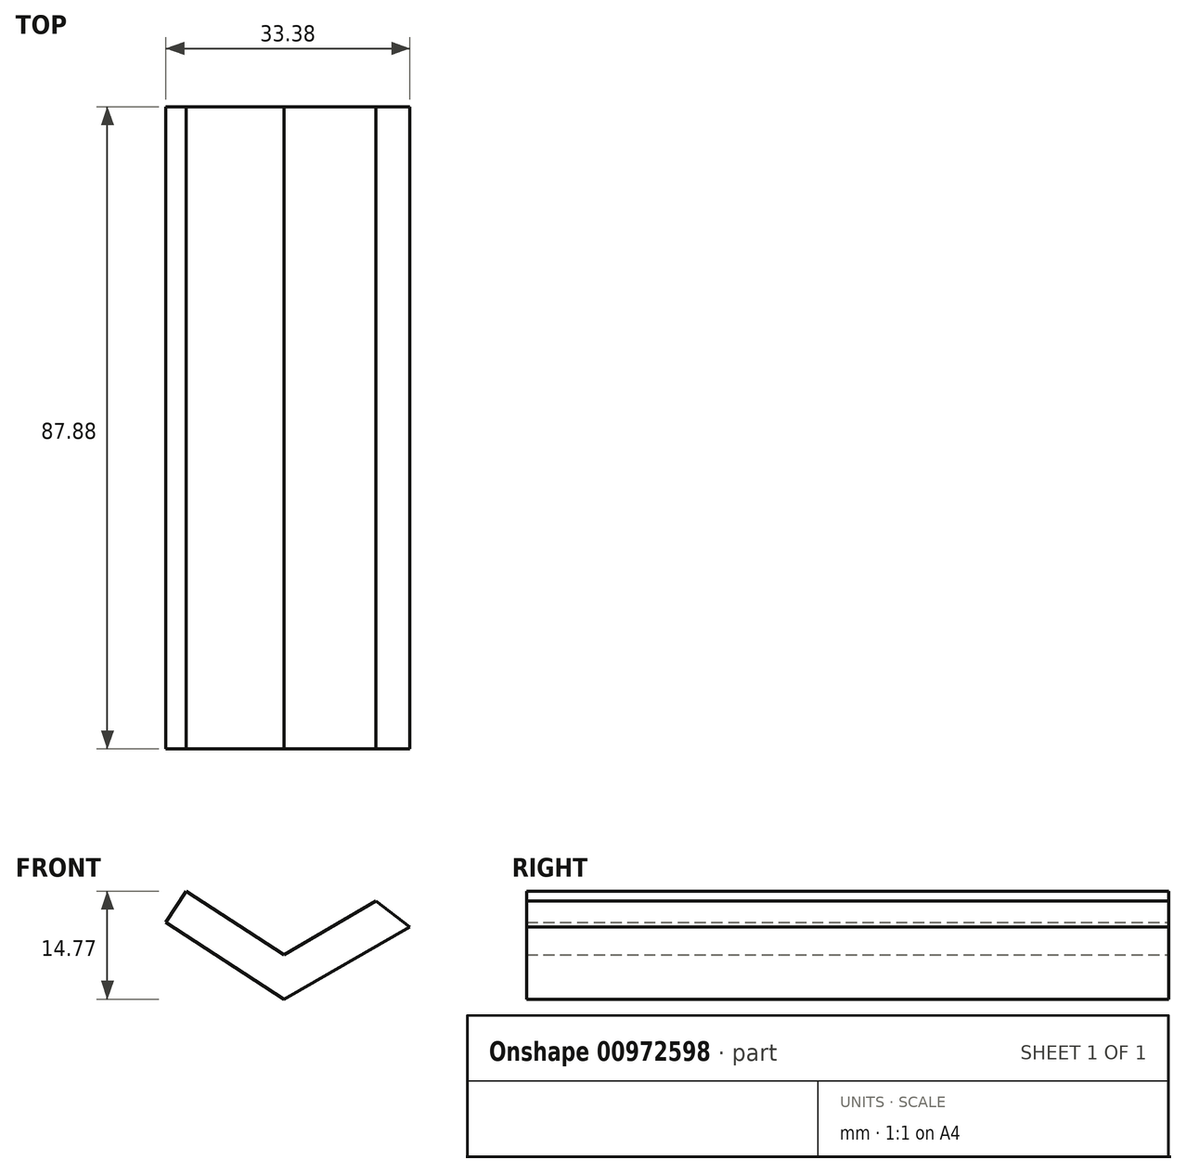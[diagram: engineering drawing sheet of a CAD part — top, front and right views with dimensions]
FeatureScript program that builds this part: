
annotation { "Feature Type Name" : "Feature", "Feature Type Description" : "" }
export const myFeature = defineFeature(function(context is Context, id is Id, definition is map)
    precondition{}
    {
        {
            var Q0;
            Q0=qCreatedBy(makeId("Front.planeOp"),FACE);
            var sketch = newSketch(context, id + "F0", { "sketchPlane" : qUnion([Q0])});
            skLineSegment(sketch, "E0", {"start": v(-25.96, 40.58) * mm, "end": v(-18.53, 35.76) * mm});
            skLineSegment(sketch, "E1", {"start": v(-25.96, 40.58) * mm, "end": v(-28.73, 36.32) * mm});
            skLineSegment(sketch, "E2", {"start": v(-28.73, 36.32) * mm, "end": v(-12.54, 25.81) * mm});
            skLineSegment(sketch, "E3", {"start": v(-12.54, 25.81) * mm, "end": v(4.65, 35.7) * mm});
            skLineSegment(sketch, "E4", {"start": v(4.65, 35.7) * mm, "end": v(0, 39.24) * mm});
            skLineSegment(sketch, "E5", {"start": v(-18.53, 35.76) * mm, "end": v(-12.54, 31.87) * mm});
            skLineSegment(sketch, "E6", {"start": v(-12.54, 31.87) * mm, "end": v(0, 39.24) * mm});
            skSolve(sketch);
        }
        {
            var Q0;
            Q0 = qSketchRegion(id + "F0", true);
            extrude(context, id + "F1", {"entities" : qUnion([Q0]), "depth" : 87.88 * mm, "offsetDistance" : 25.4 * mm});
        }
    });
